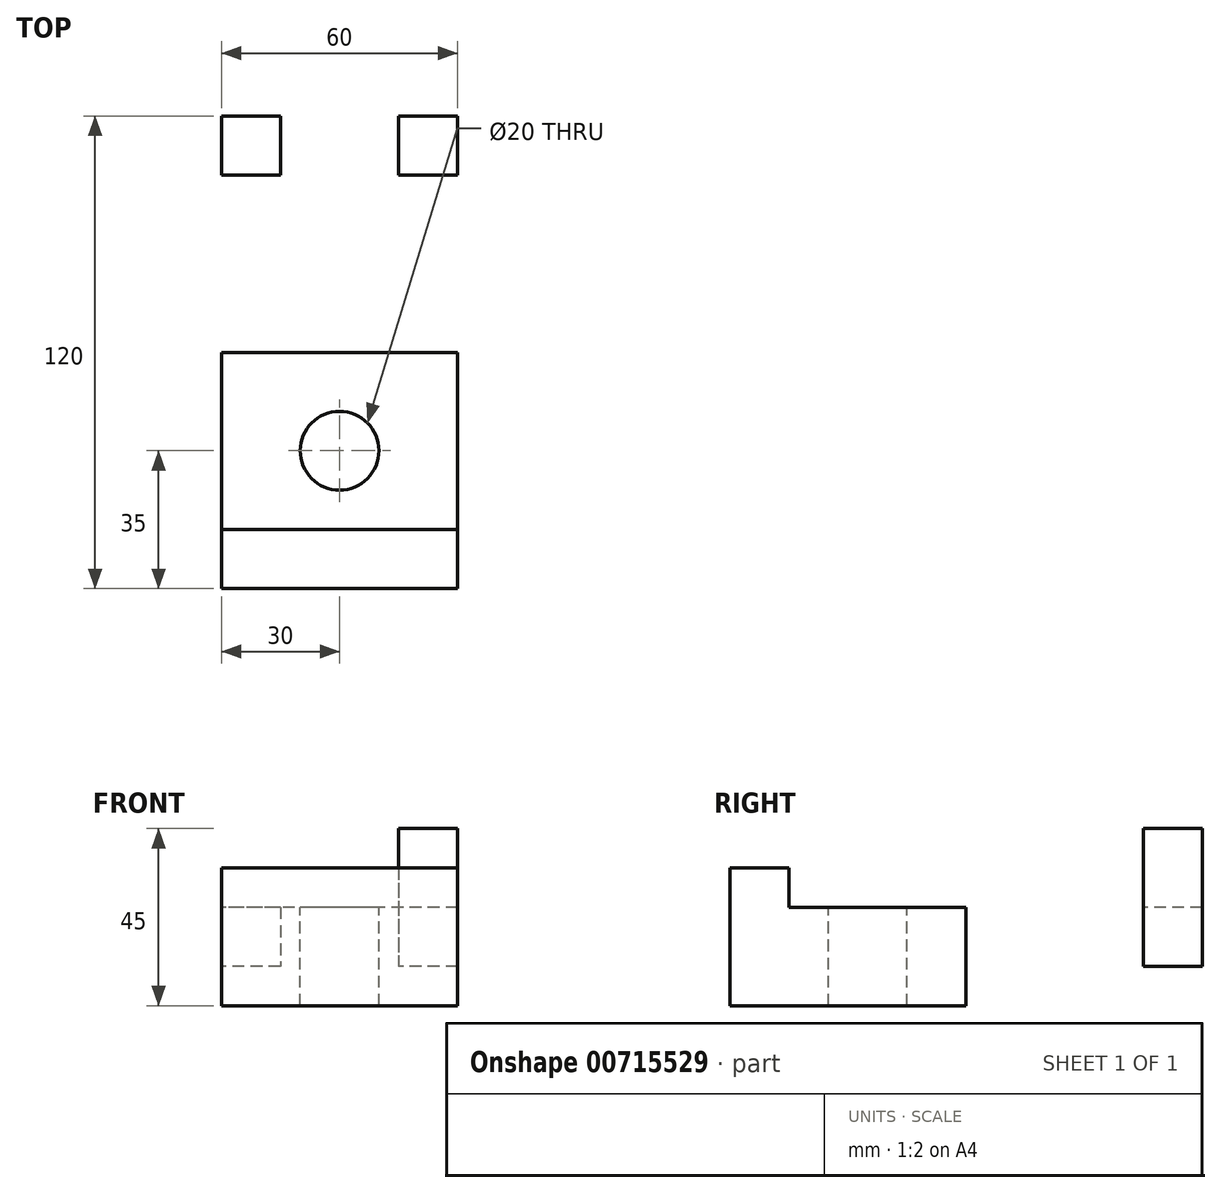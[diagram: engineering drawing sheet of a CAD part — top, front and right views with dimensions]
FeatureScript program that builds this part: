
annotation { "Feature Type Name" : "Feature", "Feature Type Description" : "" }
export const myFeature = defineFeature(function(context is Context, id is Id, definition is map)
    precondition{}
    {
        {
            var Q0;
            Q0=qCreatedBy(makeId("Top.planeOp"),FACE);
            var sketch = newSketch(context, id + "F0", { "sketchPlane" : qUnion([Q0])});
            skLineSegment(sketch, "E0.bottom", {"start": v(30, 60) * mm, "end": v(-30, 60) * mm});
            skLineSegment(sketch, "E0.top", {"start": v(30, -60) * mm, "end": v(-30, -60) * mm});
            skLineSegment(sketch, "E0.left", {"start": v(30, 60) * mm, "end": v(30, -60) * mm});
            skLineSegment(sketch, "E0.right", {"start": v(-30, 60) * mm, "end": v(-30, -60) * mm});
            skPoint(sketch, "E0.middle", {"position": v(0, 0) * mm});
            skLineSegment(sketch, "E1", {"start": v(30, -45) * mm, "end": v(-30, -45) * mm});
            skLineSegment(sketch, "E2.bottom", {"start": v(-30, 60) * mm, "end": v(-15, 60) * mm});
            skLineSegment(sketch, "E2.top", {"start": v(-30, 45) * mm, "end": v(-15, 45) * mm});
            skLineSegment(sketch, "E2.left", {"start": v(-30, 60) * mm, "end": v(-30, 45) * mm});
            skLineSegment(sketch, "E2.right", {"start": v(-15, 60) * mm, "end": v(-15, 45) * mm});
            skLineSegment(sketch, "E3.bottom", {"start": v(30, 60) * mm, "end": v(15, 60) * mm});
            skLineSegment(sketch, "E3.top", {"start": v(30, 45) * mm, "end": v(15, 45) * mm});
            skLineSegment(sketch, "E3.left", {"start": v(30, 60) * mm, "end": v(30, 45) * mm});
            skLineSegment(sketch, "E3.right", {"start": v(15, 60) * mm, "end": v(15, 45) * mm});
            skLineSegment(sketch, "E4", {"start": v(30, 0) * mm, "end": v(-30, 0) * mm});
            skSolve(sketch);
        }
        {
            var Q0;
            {var subQ0=sQuery(id+"F0.wireOp",EDGE,"E0.top");Q0=makeQuery(id+"F0.imprint","IMPRINT",FACE,{"disambiguationData":[TD([[makeQuery(id+"F0.imprint","IMPRINT",EDGE,{"derivedFrom":subQ0}),-1.0]])]});}
            var Q1;
            {var subQ0=sQuery(id+"F0.wireOp",EDGE,"E1");Q1=makeQuery(id+"F0.imprint","IMPRINT",FACE,{"disambiguationData":[TD([[makeQuery(id+"F0.imprint","IMPRINT",EDGE,{"derivedFrom":subQ0}),-1.0]])]});}
            extrude(context, id + "F1", {"entities" : qUnion([Q0, Q1]), "oppositeDirection" : true, "depth" : 10 * mm, "offsetDistance" : 25 * mm});
        }
        {
            var Q0;
            {var subQ0=sQuery(id+"F0.wireOp",EDGE,"E0.top");Q0=makeQuery(id+"F0.imprint","IMPRINT",FACE,{"disambiguationData":[TD([[makeQuery(id+"F0.imprint","IMPRINT",EDGE,{"derivedFrom":subQ0}),-1.0]])]});}
            extrude(context, id + "F2", {"entities" : qUnion([Q0]), "operationType" : NewBodyOperationType.ADD, "depth" : 25 * mm, "offsetDistance" : 25 * mm});
        }
        {
            var Q0;
            {var subQ0=sQuery(id+"F0.wireOp",EDGE,"E1");Q0=makeQuery(id+"F0.imprint","IMPRINT",FACE,{"disambiguationData":[TD([[makeQuery(id+"F0.imprint","IMPRINT",EDGE,{"derivedFrom":subQ0}),-1.0]])]});}
            extrude(context, id + "F3", {"entities" : qUnion([Q0]), "operationType" : NewBodyOperationType.ADD, "depth" : 15 * mm, "offsetDistance" : 25 * mm});
        }
        {
            var Q0;
            Q0=makeQuery(id+"F0.imprint","IMPRINT",FACE,{"disambiguationData":[TD([[makeQuery(id+"F0.imprint","IMPRINT",EDGE,{"derivedFrom":sQuery(id+"F0.wireOp",EDGE,"E3.bottom")}),1.0]])]});
            var Q1;
            Q1=makeQuery(id+"F0.imprint","IMPRINT",FACE,{"disambiguationData":[TD([[makeQuery(id+"F0.imprint","IMPRINT",EDGE,{"derivedFrom":sQuery(id+"F0.wireOp",EDGE,"E0.bottom")}),1.0]])]});
            var Q2;
            Q2=makeQuery(id+"F0.imprint","IMPRINT",FACE,{"disambiguationData":[TD([[makeQuery(id+"F0.imprint","IMPRINT",EDGE,{"derivedFrom":sQuery(id+"F0.wireOp",EDGE,"E2.bottom")}),-1.0]])]});
            var Q3;
            Q3=makeQuery(id+"F3.opExtrude","CAP_FACE",FACE,{"disambiguationData":[OSD([sQuery(id+"F0.wireOp",EDGE,"E0.left"),sQuery(id+"F0.wireOp",EDGE,"E0.right"),sQuery(id+"F0.wireOp",EDGE,"E1"),sQuery(id+"F0.wireOp",EDGE,"E4")])],"isStart":false});
            extrude(context, id + "F4", {"entities" : qUnion([Q0, Q1, Q2]), "operationType" : NewBodyOperationType.ADD, "endBound" : BoundingType.UP_TO_SURFACE, "depth" : 25 * mm, "endBoundEntityFace" : qUnion([Q3]), "offsetDistance" : 25 * mm});
        }
        {
            var Q0;
            {var subQ0=sQuery(id+"F0.wireOp",EDGE,"E4");var subQ1=sQuery(id+"F0.wireOp",EDGE,"E1");var subQ2=sQuery(id+"F0.wireOp",EDGE,"E0.right");var subQ3=sQuery(id+"F0.wireOp",EDGE,"E0.left");Q0=makeQuery(id+"F4.boolean.opBoolean","MERGE",FACE,{"derivedFrom":[makeQuery(id+"F3.opExtrude","CAP_FACE",FACE,{"disambiguationData":[OSD([subQ3,subQ2,subQ1,subQ0])],"isStart":false}),makeQuery(id+"F4.opExtrude","CAP_FACE",FACE,{"disambiguationData":[OSD([subQ3,subQ2,subQ1,subQ0])],"isStart":false})]});}
            var sketch = newSketch(context, id + "F5", { "sketchPlane" : qUnion([Q0])});
            skLineSegment(sketch, "E5.bottom", {"start": v(-30, 60) * mm, "end": v(-15, 60) * mm});
            skLineSegment(sketch, "E5.top", {"start": v(-30, 45) * mm, "end": v(-15, 45) * mm});
            skLineSegment(sketch, "E5.left", {"start": v(-30, 60) * mm, "end": v(-30, 45) * mm});
            skLineSegment(sketch, "E5.right", {"start": v(-15, 60) * mm, "end": v(-15, 45) * mm});
            skLineSegment(sketch, "E6.bottom", {"start": v(30, 60) * mm, "end": v(15, 60) * mm});
            skLineSegment(sketch, "E6.top", {"start": v(30, 45) * mm, "end": v(15, 45) * mm});
            skLineSegment(sketch, "E6.left", {"start": v(30, 60) * mm, "end": v(30, 45) * mm});
            skLineSegment(sketch, "E6.right", {"start": v(15, 60) * mm, "end": v(15, 45) * mm});
            skSolve(sketch);
        }
        {
            var Q0;
            Q0=makeQuery(id+"F5.imprint","IMPRINT",FACE,{"disambiguationData":[TD([[makeQuery(id+"F5.imprint","IMPRINT",EDGE,{"derivedFrom":sQuery(id+"F5.wireOp",EDGE,"E5.bottom")}),1.0]])]});
            var Q1;
            Q1=makeQuery(id+"F5.imprint","IMPRINT",FACE,{"disambiguationData":[TD([[makeQuery(id+"F5.imprint","IMPRINT",EDGE,{"derivedFrom":sQuery(id+"F5.wireOp",EDGE,"E6.bottom")}),1.0]])]});
            extrude(context, id + "F6", {"entities" : qUnion([Q0, Q1]), "operationType" : NewBodyOperationType.ADD, "depth" : 20 * mm, "offsetDistance" : 25 * mm});
        }
        {
            var Q0;
            {var subQ0=sQuery(id+"F0.wireOp",EDGE,"E4");var subQ1=sQuery(id+"F0.wireOp",EDGE,"E1");var subQ2=sQuery(id+"F0.wireOp",EDGE,"E0.right");var subQ3=sQuery(id+"F0.wireOp",EDGE,"E0.left");Q0=makeQuery(id+"F4.boolean.opBoolean","MERGE",FACE,{"derivedFrom":[makeQuery(id+"F3.opExtrude","CAP_FACE",FACE,{"disambiguationData":[OSD([subQ3,subQ2,subQ1,subQ0])],"isStart":false}),makeQuery(id+"F4.opExtrude","CAP_FACE",FACE,{"disambiguationData":[OSD([subQ3,subQ2,subQ1,subQ0])],"isStart":false})]});}
            var sketch = newSketch(context, id + "F7", { "sketchPlane" : qUnion([Q0])});
            skLineSegment(sketch, "E7", {"start": v(0, -45) * mm, "end": v(0, -25) * mm});
            skCircle(sketch, "E8", {"center": v(0, -25) * mm, "radius": 10 * mm});
            skLineSegment(sketch, "E9", {"start": v(0, -25) * mm, "end": v(0, 20) * mm});
            skCircle(sketch, "E10", {"center": v(0, 20) * mm, "radius": 10 * mm});
            skSolve(sketch);
        }
        {
            var Q0;
            Q0=makeQuery(id+"F7.imprint","IMPRINT",FACE,{"disambiguationData":[TD([[makeQuery(id+"F7.imprint","IMPRINT",EDGE,{"derivedFrom":sQuery(id+"F7.wireOp",EDGE,"E10")}),1.0]])]});
            var Q1;
            {var subQ0=sQuery(id+"F7.wireOp",EDGE,"E9");var subQ1=sQuery(id+"F7.wireOp",EDGE,"E7");var subQ2=makeQuery(id+"F7.imprint","INTERSECT",VERTEX,{"derivedFrom":[subQ1,subQ0]});Q1=makeQuery(id+"F7.imprint","IMPRINT",FACE,{"disambiguationData":[TD([[makeQuery(id+"F7.imprint","IMPRINT",EDGE,{"disambiguationData":[TD([[subQ2,1.0]])],"derivedFrom":subQ1}),-1.0]])]});}
            var Q2;
            {var subQ0=sQuery(id+"F7.wireOp",EDGE,"E9");var subQ1=sQuery(id+"F7.wireOp",EDGE,"E7");var subQ2=makeQuery(id+"F7.imprint","INTERSECT",VERTEX,{"derivedFrom":[subQ1,subQ0]});Q2=makeQuery(id+"F7.imprint","IMPRINT",FACE,{"disambiguationData":[TD([[makeQuery(id+"F7.imprint","IMPRINT",EDGE,{"disambiguationData":[TD([[subQ2,1.0]])],"derivedFrom":subQ1}),1.0]])]});}
            extrude(context, id + "F8", {"entities" : qUnion([Q0, Q1, Q2]), "operationType" : NewBodyOperationType.REMOVE, "oppositeDirection" : true, "depth" : 40 * mm, "offsetDistance" : 25 * mm});
        }
    });
